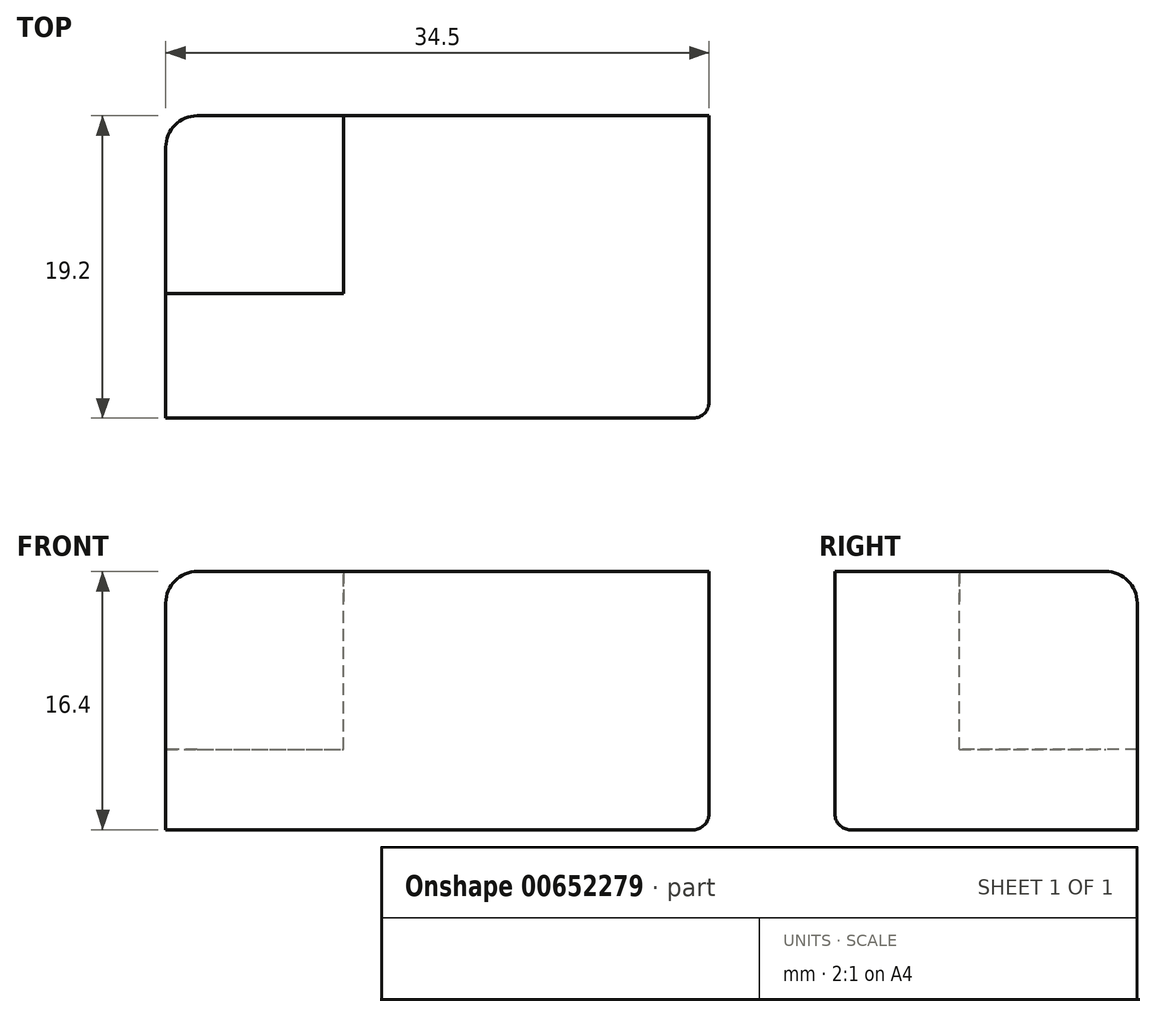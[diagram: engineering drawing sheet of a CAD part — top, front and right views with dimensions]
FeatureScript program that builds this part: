
annotation { "Feature Type Name" : "Feature", "Feature Type Description" : "" }
export const myFeature = defineFeature(function(context is Context, id is Id, definition is map)
    precondition{}
    {
        {
            var Q0;
            Q0=qCreatedBy(makeId("Top.planeOp"),FACE);
            var sketch = newSketch(context, id + "F0", { "sketchPlane" : qUnion([Q0])});
            skLineSegment(sketch, "E0.bottom", {"start": v(0, 0) * mm, "end": v(34.5, 0) * mm});
            skLineSegment(sketch, "E0.top", {"start": v(0, 19.2) * mm, "end": v(34.5, 19.2) * mm});
            skLineSegment(sketch, "E0.left", {"start": v(0, 0) * mm, "end": v(0, 19.2) * mm});
            skLineSegment(sketch, "E0.right", {"start": v(34.5, 0) * mm, "end": v(34.5, 19.2) * mm});
            skSolve(sketch);
        }
        {
            var Q0;
            Q0=makeQuery(id+"F0.imprint","IMPRINT",FACE,{"disambiguationData":[TD([[makeQuery(id+"F0.imprint","IMPRINT",EDGE,{"derivedFrom":sQuery(id+"F0.wireOp",EDGE,"E0.bottom")}),1.0]])]});
            extrude(context, id + "F1", {"entities" : qUnion([Q0]), "depth" : 16.4 * mm, "offsetDistance" : 25 * mm});
        }
        {
            var Q0;
            Q0=makeQuery(id+"F1.opExtrude","CAP_FACE",FACE,{"disambiguationData":[OSD([sQuery(id+"F0.wireOp",EDGE,"E0.bottom"),sQuery(id+"F0.wireOp",EDGE,"E0.top"),sQuery(id+"F0.wireOp",EDGE,"E0.left"),sQuery(id+"F0.wireOp",EDGE,"E0.right")])],"isStart":false});
            var sketch = newSketch(context, id + "F2", { "sketchPlane" : qUnion([Q0])});
            skLineSegment(sketch, "E1.bottom", {"start": v(0, 19.2) * mm, "end": v(11.3, 19.2) * mm});
            skLineSegment(sketch, "E1.top", {"start": v(0, 7.9) * mm, "end": v(11.3, 7.9) * mm});
            skLineSegment(sketch, "E1.left", {"start": v(0, 19.2) * mm, "end": v(0, 7.9) * mm});
            skLineSegment(sketch, "E1.right", {"start": v(11.3, 19.2) * mm, "end": v(11.3, 7.9) * mm});
            skSolve(sketch);
        }
        {
            var Q0;
            Q0=makeQuery(id+"F2.imprint","IMPRINT",FACE,{"disambiguationData":[TD([[makeQuery(id+"F2.imprint","IMPRINT",EDGE,{"derivedFrom":sQuery(id+"F2.wireOp",EDGE,"E1.bottom")}),-1.0]])]});
            extrude(context, id + "F3", {"entities" : qUnion([Q0]), "operationType" : NewBodyOperationType.REMOVE, "oppositeDirection" : true, "depth" : 11.3 * mm, "offsetDistance" : 25 * mm});
        }
        {
            var Q0;
            Q0=makeQuery(id+"F1.opExtrude","SWEPT_EDGE",EDGE,{"disambiguationData":[OSD([sQuery(id+"F0.wireOp",EDGE,"E0.bottom"),sQuery(id+"F0.wireOp",EDGE,"E0.right")])]});
            var Q1;
            Q1=makeQuery(id+"F1.opExtrude","CAP_EDGE",EDGE,{"disambiguationData":[OSD([sQuery(id+"F0.wireOp",EDGE,"E0.right")])],"isStart":true});
            var Q2;
            Q2=makeQuery(id+"F1.opExtrude","CAP_EDGE",EDGE,{"disambiguationData":[OSD([sQuery(id+"F0.wireOp",EDGE,"E0.bottom")])],"isStart":true});
            fillet(context, id + "F4", {"entities" : qUnion([Q0, Q1, Q2]), "radius" : 1 * mm, "tangentPropagation" : true, "allowEdgeOverflow" : false});
        }
        {
            var Q0;
            Q0=makeQuery(id+"F1.opExtrude","SWEPT_EDGE",EDGE,{"disambiguationData":[OSD([sQuery(id+"F0.wireOp",EDGE,"E0.top"),sQuery(id+"F0.wireOp",EDGE,"E0.left")])]});
            var Q1;
            Q1=makeQuery(id+"F1.opExtrude","CAP_EDGE",EDGE,{"disambiguationData":[OSD([sQuery(id+"F0.wireOp",EDGE,"E0.left")])],"isStart":false});
            var Q2;
            Q2=makeQuery(id+"F1.opExtrude","CAP_EDGE",EDGE,{"disambiguationData":[OSD([sQuery(id+"F0.wireOp",EDGE,"E0.top")])],"isStart":false});
            fillet(context, id + "F5", {"entities" : qUnion([Q0, Q1, Q2]), "radius" : 2 * mm, "tangentPropagation" : true, "allowEdgeOverflow" : false});
        }
    });
